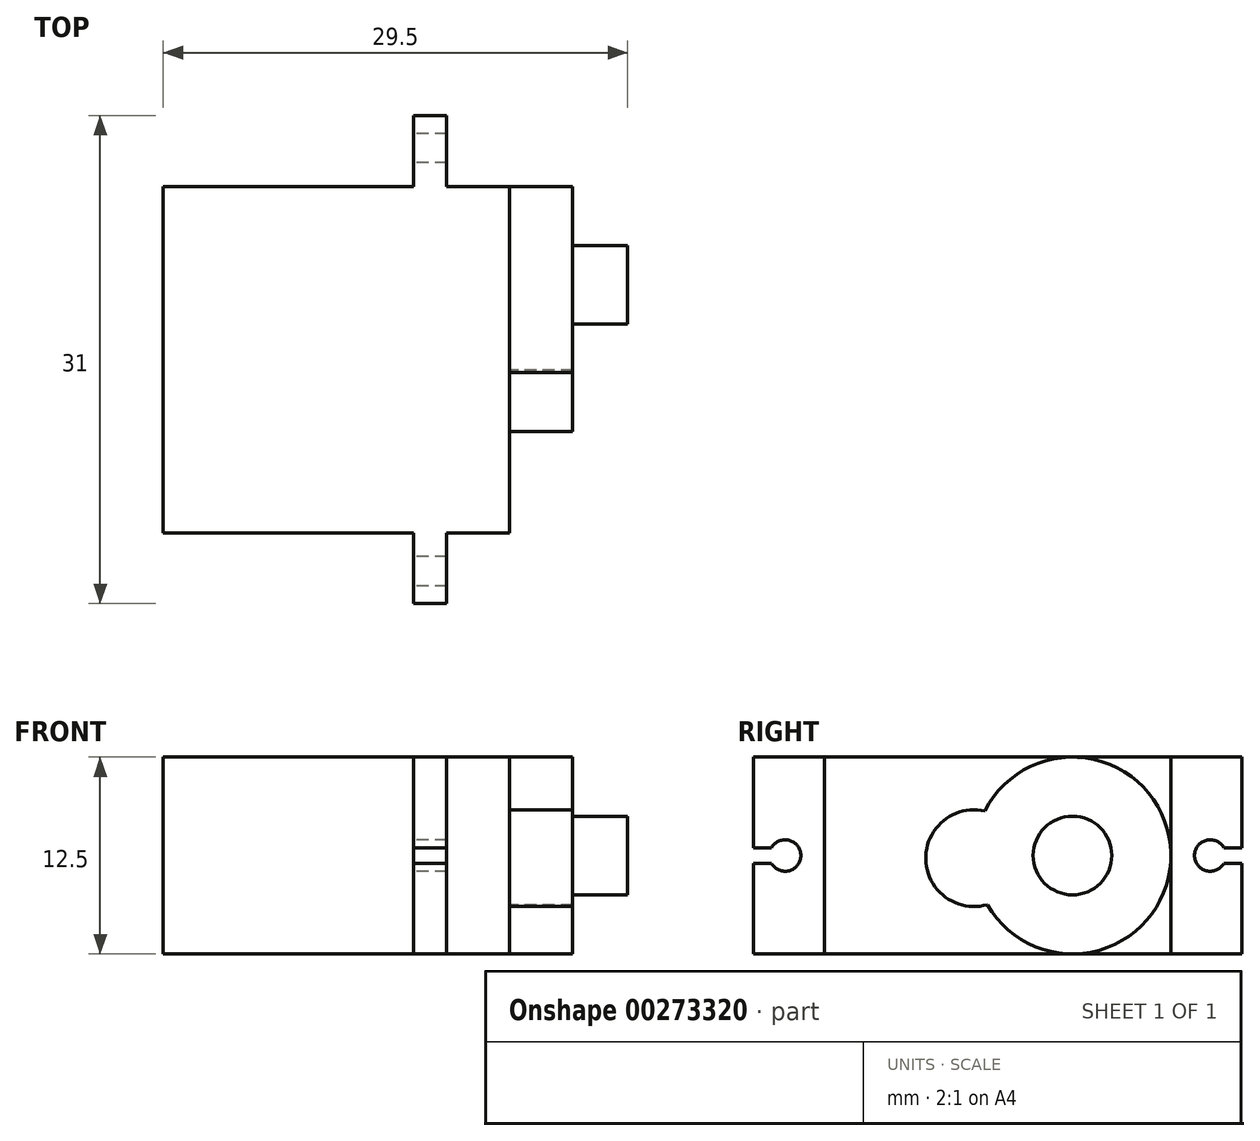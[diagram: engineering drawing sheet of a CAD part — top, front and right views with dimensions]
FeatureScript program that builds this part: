
annotation { "Feature Type Name" : "Feature", "Feature Type Description" : "" }
export const myFeature = defineFeature(function(context is Context, id is Id, definition is map)
    precondition{}
    {
        {
            var Q0;
            Q0=qCreatedBy(makeId("Top.planeOp"),FACE);
            var sketch = newSketch(context, id + "F0", { "sketchPlane" : qUnion([Q0])});
            skLineSegment(sketch, "E0.bottom", {"start": v(11, 11) * mm, "end": v(-11, 11) * mm});
            skLineSegment(sketch, "E0.top", {"start": v(11, -11) * mm, "end": v(-11, -11) * mm});
            skLineSegment(sketch, "E0.left", {"start": v(11, 11) * mm, "end": v(11, -11) * mm});
            skLineSegment(sketch, "E0.right", {"start": v(-11, 11) * mm, "end": v(-11, -11) * mm});
            skPoint(sketch, "E0.middle", {"position": v(0, 0) * mm});
            skSolve(sketch);
        }
        {
            var Q0;
            Q0=makeQuery(id+"F0.imprint","IMPRINT",FACE,{"disambiguationData":[TD([[makeQuery(id+"F0.imprint","IMPRINT",EDGE,{"derivedFrom":sQuery(id+"F0.wireOp",EDGE,"E0.bottom")}),1.0]])]});
            extrude(context, id + "F1", {"entities" : qUnion([Q0]), "depth" : 12.5 * mm});
        }
        {
            var Q0;
            Q0=makeQuery(id+"F1.opExtrude","SWEPT_FACE",FACE,{"disambiguationData":[OSD([sQuery(id+"F0.wireOp",EDGE,"E0.left")])]});
            var sketch = newSketch(context, id + "F2", { "sketchPlane" : qUnion([Q0])});
            skLineSegment(sketch, "E1.0.0", {"start": v(-11, 0) * mm, "end": v(11, 0) * mm});
            skLineSegment(sketch, "E1.0.1", {"start": v(11, 0) * mm, "end": v(11, 12.5) * mm});
            skLineSegment(sketch, "E1.0.2", {"start": v(11, 12.5) * mm, "end": v(-11, 12.5) * mm});
            skLineSegment(sketch, "E1.0.3", {"start": v(-11, 12.5) * mm, "end": v(-11, 0) * mm});
            skLineSegment(sketch, "E2.bottom", {"start": v(-11, 12.5) * mm, "end": v(10.4, 12.5) * mm});
            skLineSegment(sketch, "E2.top", {"start": v(-11, 0) * mm, "end": v(10.4, 0) * mm});
            skCircle(sketch, "E3", {"center": v(4.75, 6.25) * mm, "radius": 6.25 * mm});
            skCircle(sketch, "E4", {"center": v(-1.5, 6.08) * mm, "radius": 3.07 * mm});
            skSolve(sketch);
        }
        {
            var Q0;
            {var subQ0=sQuery(id+"F2.wireOp",EDGE,"E3");var subQ1=makeQuery(id+"F2.imprint","INTERSECT",VERTEX,{"derivedFrom":[sQuery(id+"F2.wireOp",EDGE,"E1.0.1"),subQ0]});Q0=makeQuery(id+"F2.imprint","IMPRINT",FACE,{"disambiguationData":[TD([[makeQuery(id+"F2.imprint","IMPRINT",EDGE,{"disambiguationData":[TD([[subQ1,-1.0]])],"derivedFrom":subQ0}),1.0]])]});}
            var Q1;
            {var subQ0=sQuery(id+"F2.wireOp",EDGE,"E4");var subQ1=sQuery(id+"F2.wireOp",EDGE,"E3");var subQ2=makeQuery(id+"F2.imprint","INTERSECT",VERTEX,{"disambiguationData":[OD(0.0)],"derivedFrom":[subQ1,subQ0]});Q1=makeQuery(id+"F2.imprint","IMPRINT",FACE,{"disambiguationData":[TD([[makeQuery(id+"F2.imprint","IMPRINT",EDGE,{"disambiguationData":[TD([[subQ2,-1.0]])],"derivedFrom":subQ1}),-1.0]])]});}
            var Q2;
            {var subQ0=sQuery(id+"F2.wireOp",EDGE,"E4");var subQ1=sQuery(id+"F2.wireOp",EDGE,"E3");var subQ2=makeQuery(id+"F2.imprint","INTERSECT",VERTEX,{"disambiguationData":[OD(0.0)],"derivedFrom":[subQ1,subQ0]});Q2=makeQuery(id+"F2.imprint","IMPRINT",FACE,{"disambiguationData":[TD([[makeQuery(id+"F2.imprint","IMPRINT",EDGE,{"disambiguationData":[TD([[subQ2,-1.0]])],"derivedFrom":subQ1}),1.0]])]});}
            extrude(context, id + "F3", {"entities" : qUnion([Q0, Q1, Q2]), "operationType" : NewBodyOperationType.ADD, "depth" : 4 * mm});
        }
        {
            var Q0;
            Q0=makeQuery(id+"F3.opExtrude","CAP_FACE",FACE,{"disambiguationData":[OSD([sQuery(id+"F2.wireOp",EDGE,"E3"),sQuery(id+"F2.wireOp",EDGE,"E4")])],"isStart":false});
            var sketch = newSketch(context, id + "F4", { "sketchPlane" : qUnion([Q0])});
            skCircle(sketch, "E5", {"center": v(4.75, 6.25) * mm, "radius": 2.5 * mm});
            skSolve(sketch);
        }
        {
            var Q0;
            Q0=makeQuery(id+"F4.imprint","IMPRINT",FACE,{"disambiguationData":[TD([[makeQuery(id+"F4.imprint","IMPRINT",EDGE,{"derivedFrom":sQuery(id+"F4.wireOp",EDGE,"E5")}),1.0]])]});
            extrude(context, id + "F5", {"entities" : qUnion([Q0]), "operationType" : NewBodyOperationType.ADD, "depth" : 3.5 * mm});
        }
        {
            var Q0;
            Q0=makeQuery(id+"F1.opExtrude","SWEPT_FACE",FACE,{"disambiguationData":[OSD([sQuery(id+"F0.wireOp",EDGE,"E0.top")])]});
            var sketch = newSketch(context, id + "F6", { "sketchPlane" : qUnion([Q0])});
            skLineSegment(sketch, "E6.bottom", {"start": v(7, 12.5) * mm, "end": v(4.9, 12.5) * mm});
            skLineSegment(sketch, "E6.top", {"start": v(7, 0) * mm, "end": v(4.9, 0) * mm});
            skLineSegment(sketch, "E6.left", {"start": v(7, 12.5) * mm, "end": v(7, 0) * mm});
            skLineSegment(sketch, "E6.right", {"start": v(4.9, 12.5) * mm, "end": v(4.9, 0) * mm});
            skSolve(sketch);
        }
        {
            var Q0;
            Q0=makeQuery(id+"F6.imprint","IMPRINT",FACE,{"disambiguationData":[TD([[makeQuery(id+"F6.imprint","IMPRINT",EDGE,{"derivedFrom":sQuery(id+"F6.wireOp",EDGE,"E6.bottom")}),1.0]])]});
            extrude(context, id + "F7", {"entities" : qUnion([Q0]), "operationType" : NewBodyOperationType.ADD, "depth" : 4.5 * mm});
        }
        {
            var Q0;
            Q0=makeQuery(id+"F7.opExtrude","SWEPT_FACE",FACE,{"disambiguationData":[OSD([sQuery(id+"F6.wireOp",EDGE,"E6.right")])]});
            var sketch = newSketch(context, id + "F8", { "sketchPlane" : qUnion([Q0])});
            skCircle(sketch, "E7", {"center": v(13.5, 6.25) * mm, "radius": 1 * mm});
            skLineSegment(sketch, "E8", {"start": v(14.37, 6.75) * mm, "end": v(15.5, 6.75) * mm});
            skLineSegment(sketch, "E9", {"start": v(14.37, 5.75) * mm, "end": v(15.5, 5.75) * mm});
            skSolve(sketch);
        }
        {
            var Q0;
            {var subQ0=sQuery(id+"F8.wireOp",EDGE,"E8");Q0=makeQuery(id+"F8.imprint","IMPRINT",FACE,{"disambiguationData":[TD([[makeQuery(id+"F8.imprint","IMPRINT",EDGE,{"derivedFrom":subQ0}),-1.0]])]});}
            var Q1;
            {var subQ0=sQuery(id+"F8.wireOp",EDGE,"E7");var subQ1=makeQuery(id+"F8.imprint","INTERSECT",VERTEX,{"derivedFrom":[subQ0,sQuery(id+"F8.wireOp",EDGE,"E8")]});Q1=makeQuery(id+"F8.imprint","IMPRINT",FACE,{"disambiguationData":[TD([[makeQuery(id+"F8.imprint","IMPRINT",EDGE,{"disambiguationData":[TD([[subQ1,-1.0]])],"derivedFrom":subQ0}),1.0]])]});}
            extrude(context, id + "F9", {"entities" : qUnion([Q0, Q1]), "operationType" : NewBodyOperationType.REMOVE, "oppositeDirection" : true, "depth" : 2.1 * mm});
        }
        {
            var Q0;
            Q0=makeQuery(id+"F1.opExtrude","SWEPT_FACE",FACE,{"disambiguationData":[OSD([sQuery(id+"F0.wireOp",EDGE,"E0.bottom")])]});
            var sketch = newSketch(context, id + "F10", { "sketchPlane" : qUnion([Q0])});
            skLineSegment(sketch, "E10.bottom", {"start": v(-7, 12.5) * mm, "end": v(-4.9, 12.5) * mm});
            skLineSegment(sketch, "E10.top", {"start": v(-7, 0) * mm, "end": v(-4.9, 0) * mm});
            skLineSegment(sketch, "E10.left", {"start": v(-7, 12.5) * mm, "end": v(-7, 0) * mm});
            skLineSegment(sketch, "E10.right", {"start": v(-4.9, 12.5) * mm, "end": v(-4.9, 0) * mm});
            skSolve(sketch);
        }
        {
            var Q0;
            Q0=makeQuery(id+"F10.imprint","IMPRINT",FACE,{"disambiguationData":[TD([[makeQuery(id+"F10.imprint","IMPRINT",EDGE,{"derivedFrom":sQuery(id+"F10.wireOp",EDGE,"E10.bottom")}),-1.0]])]});
            extrude(context, id + "F11", {"entities" : qUnion([Q0]), "operationType" : NewBodyOperationType.ADD, "depth" : 4.5 * mm});
        }
        {
            var Q0;
            Q0=makeQuery(id+"F11.opExtrude","SWEPT_FACE",FACE,{"disambiguationData":[OSD([sQuery(id+"F10.wireOp",EDGE,"E10.right")])]});
            var sketch = newSketch(context, id + "F12", { "sketchPlane" : qUnion([Q0])});
            skCircle(sketch, "E11", {"center": v(-13.5, 6.25) * mm, "radius": 1 * mm});
            skLineSegment(sketch, "E12", {"start": v(-14.37, 6.75) * mm, "end": v(-15.5, 6.75) * mm});
            skLineSegment(sketch, "E13", {"start": v(-14.37, 5.75) * mm, "end": v(-15.5, 5.75) * mm});
            skSolve(sketch);
        }
        {
            var Q0;
            {var subQ0=sQuery(id+"F12.wireOp",EDGE,"E11");var subQ1=makeQuery(id+"F12.imprint","INTERSECT",VERTEX,{"derivedFrom":[subQ0,sQuery(id+"F12.wireOp",EDGE,"E12")]});Q0=makeQuery(id+"F12.imprint","IMPRINT",FACE,{"disambiguationData":[TD([[makeQuery(id+"F12.imprint","IMPRINT",EDGE,{"disambiguationData":[TD([[subQ1,-1.0]])],"derivedFrom":subQ0}),1.0]])]});}
            var Q1;
            {var subQ0=sQuery(id+"F12.wireOp",EDGE,"E12");Q1=makeQuery(id+"F12.imprint","IMPRINT",FACE,{"disambiguationData":[TD([[makeQuery(id+"F12.imprint","IMPRINT",EDGE,{"derivedFrom":subQ0}),1.0]])]});}
            extrude(context, id + "F13", {"entities" : qUnion([Q0, Q1]), "operationType" : NewBodyOperationType.REMOVE, "oppositeDirection" : true, "depth" : 2.1 * mm});
        }
    });
